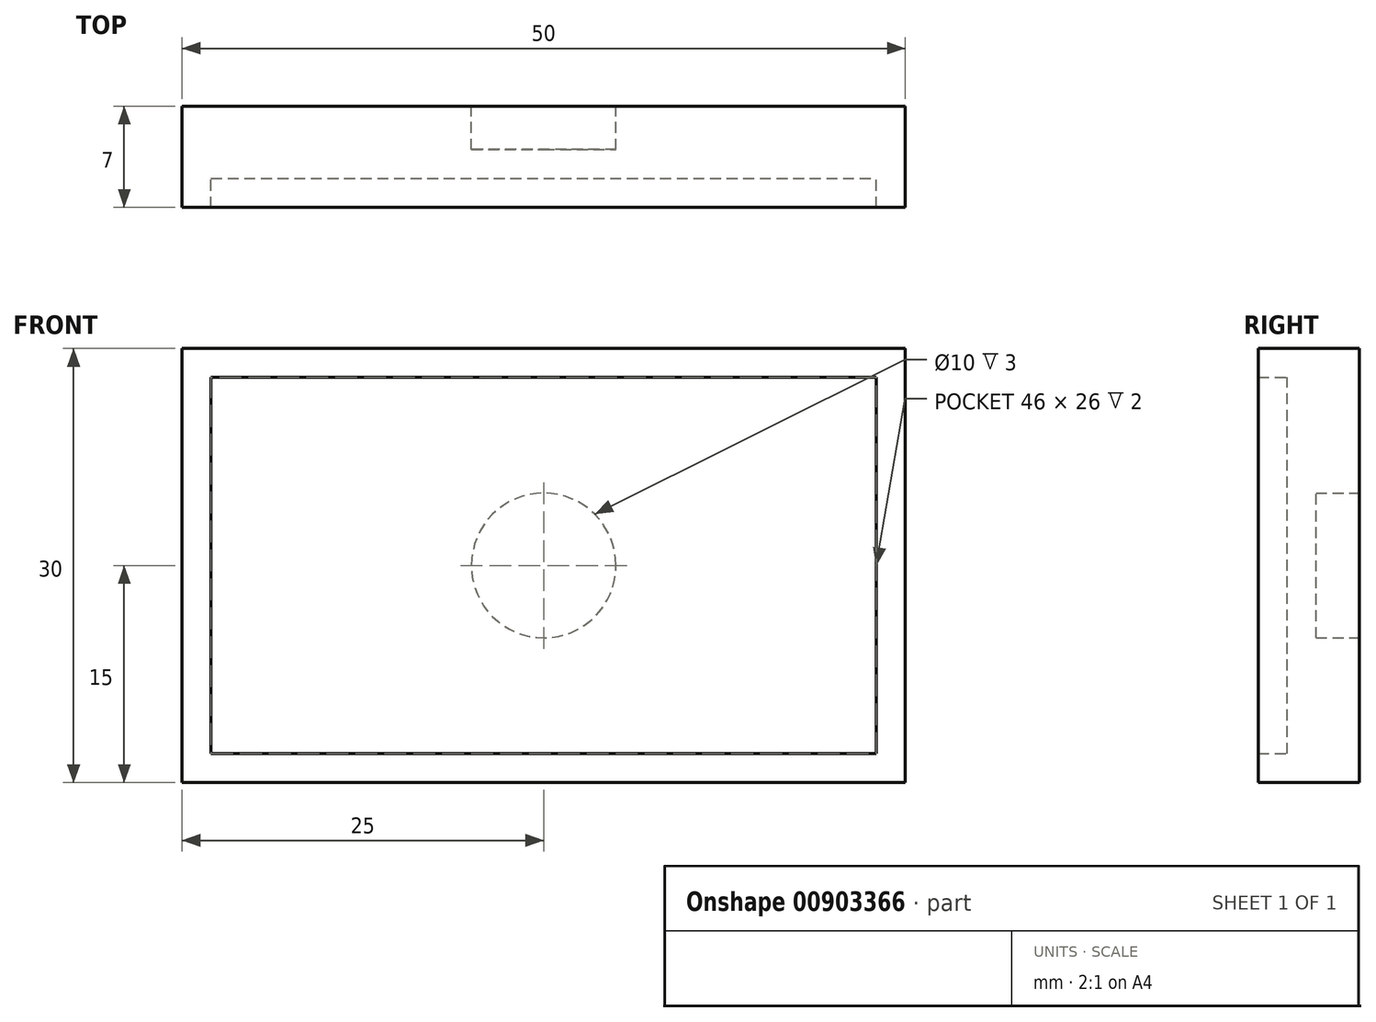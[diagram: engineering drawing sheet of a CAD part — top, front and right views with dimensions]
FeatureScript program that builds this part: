
annotation { "Feature Type Name" : "Feature", "Feature Type Description" : "" }
export const myFeature = defineFeature(function(context is Context, id is Id, definition is map)
    precondition{}
    {
        {
            var Q0;
            Q0=qCreatedBy(makeId("Front.planeOp"),FACE);
            var sketch = newSketch(context, id + "F0", { "sketchPlane" : qUnion([Q0])});
            skLineSegment(sketch, "E0.bottom", {"start": v(0, 0) * mm, "end": v(0, 0) * mm});
            skLineSegment(sketch, "E0.top", {"start": v(0, 0) * mm, "end": v(0, 0) * mm});
            skLineSegment(sketch, "E0.left", {"start": v(0, 0) * mm, "end": v(0, 0) * mm});
            skLineSegment(sketch, "E0.right", {"start": v(0, 0) * mm, "end": v(0, 0) * mm});
            skPoint(sketch, "E0.middle", {"position": v(0, 0) * mm});
            skLineSegment(sketch, "E1.bottom", {"start": v(25, 15) * mm, "end": v(-25, 15) * mm});
            skLineSegment(sketch, "E1.top", {"start": v(25, -15) * mm, "end": v(-25, -15) * mm});
            skLineSegment(sketch, "E1.left", {"start": v(25, 15) * mm, "end": v(25, -15) * mm});
            skLineSegment(sketch, "E1.right", {"start": v(-25, 15) * mm, "end": v(-25, -15) * mm});
            skLineSegment(sketch, "E2.0", {"start": v(23, 13) * mm, "end": v(-23, 13) * mm});
            skLineSegment(sketch, "E2.1", {"start": v(23, 13) * mm, "end": v(23, -13) * mm});
            skLineSegment(sketch, "E2.2", {"start": v(23, -13) * mm, "end": v(-23, -13) * mm});
            skLineSegment(sketch, "E2.3", {"start": v(-23, 13) * mm, "end": v(-23, -13) * mm});
            skCircle(sketch, "E3", {"center": v(0, 0) * mm, "radius": 8 * mm});
            skCircle(sketch, "E4.0", {"center": v(0, 0) * mm, "radius": 5 * mm});
            skSolve(sketch);
        }
        {
            var Q0;
            Q0=makeQuery(id+"F0.imprint","IMPRINT",FACE,{"disambiguationData":[TD([[makeQuery(id+"F0.imprint","IMPRINT",EDGE,{"derivedFrom":sQuery(id+"F0.wireOp",EDGE,"E1.bottom")}),1.0]])]});
            var Q1;
            Q1=makeQuery(id+"F0.imprint","IMPRINT",FACE,{"disambiguationData":[TD([[makeQuery(id+"F0.imprint","IMPRINT",EDGE,{"derivedFrom":sQuery(id+"F0.wireOp",EDGE,"E2.0")}),1.0]])]});
            var Q2;
            Q2=makeQuery(id+"F0.imprint","IMPRINT",FACE,{"disambiguationData":[TD([[makeQuery(id+"F0.imprint","IMPRINT",EDGE,{"derivedFrom":sQuery(id+"F0.wireOp",EDGE,"E4.0")}),1.0]])]});
            var Q3;
            Q3=makeQuery(id+"F0.imprint","IMPRINT",FACE,{"disambiguationData":[TD([[makeQuery(id+"F0.imprint","IMPRINT",EDGE,{"derivedFrom":sQuery(id+"F0.wireOp",EDGE,"E3")}),1.0]])]});
            extrude(context, id + "F1", {"entities" : qUnion([Q0, Q1, Q2, Q3]), "depth" : 5 * mm, "offsetDistance" : 25 * mm});
        }
        {
            var Q0;
            Q0=makeQuery(id+"F0.imprint","IMPRINT",FACE,{"disambiguationData":[TD([[makeQuery(id+"F0.imprint","IMPRINT",EDGE,{"derivedFrom":sQuery(id+"F0.wireOp",EDGE,"E1.bottom")}),1.0]])]});
            extrude(context, id + "F2", {"entities" : qUnion([Q0]), "operationType" : NewBodyOperationType.ADD, "depth" : 7 * mm, "offsetDistance" : 25 * mm});
        }
        {
            var Q0;
            Q0=makeQuery(id+"F0.imprint","IMPRINT",FACE,{"disambiguationData":[TD([[makeQuery(id+"F0.imprint","IMPRINT",EDGE,{"derivedFrom":sQuery(id+"F0.wireOp",EDGE,"E4.0")}),1.0]])]});
            extrude(context, id + "F3", {"entities" : qUnion([Q0]), "operationType" : NewBodyOperationType.REMOVE, "depth" : 3 * mm, "offsetDistance" : 25 * mm});
        }
    });
